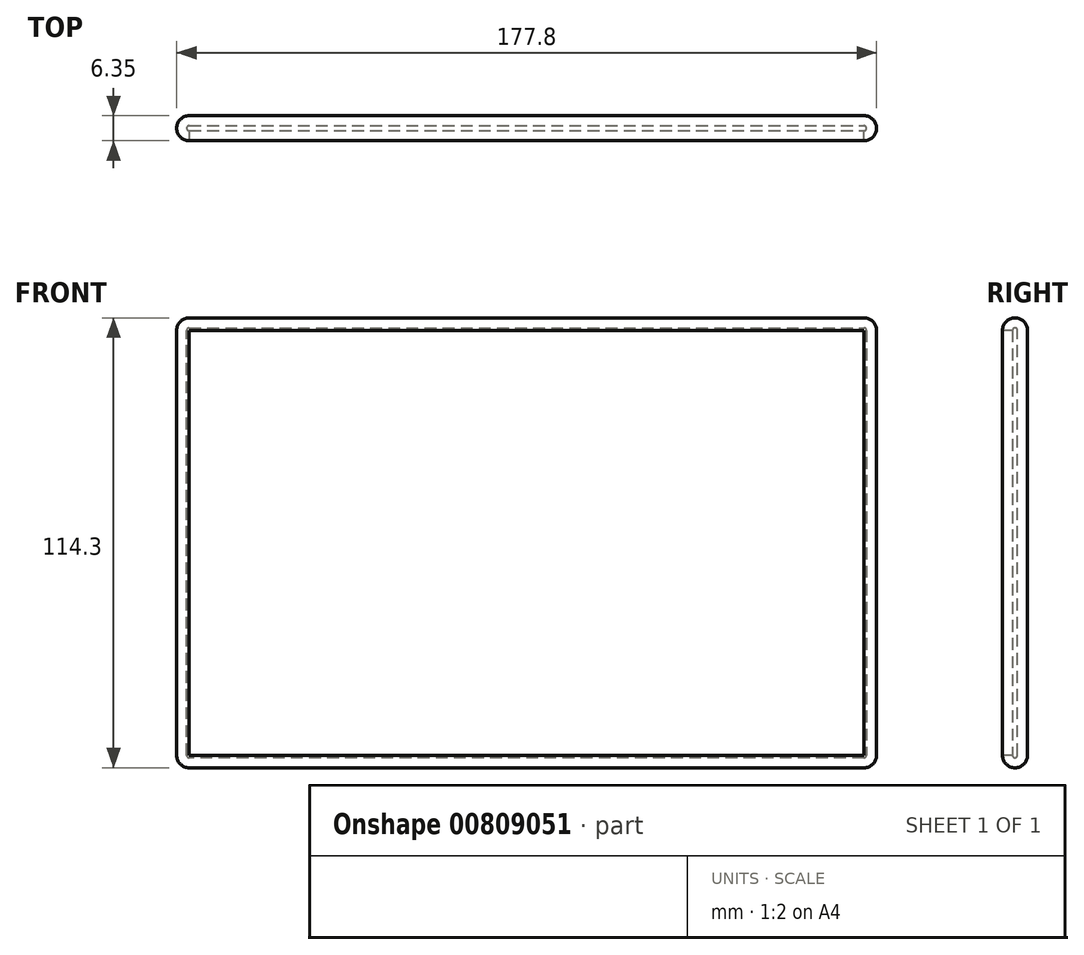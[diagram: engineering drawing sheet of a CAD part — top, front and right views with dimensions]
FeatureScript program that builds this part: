
annotation { "Feature Type Name" : "Feature", "Feature Type Description" : "" }
export const myFeature = defineFeature(function(context is Context, id is Id, definition is map)
    precondition{}
    {
        {
            var Q0;
            Q0=qCreatedBy(makeId("Front.planeOp"),FACE);
            var sketch = newSketch(context, id + "F0", { "sketchPlane" : qUnion([Q0])});
            skLineSegment(sketch, "E0.bottom", {"start": v(-42.92, 86.07) * mm, "end": v(134.88, 86.07) * mm});
            skLineSegment(sketch, "E0.top", {"start": v(-42.92, -28.23) * mm, "end": v(134.88, -28.23) * mm});
            skLineSegment(sketch, "E0.left", {"start": v(-42.92, 86.07) * mm, "end": v(-42.92, -28.23) * mm});
            skLineSegment(sketch, "E0.right", {"start": v(134.88, 86.07) * mm, "end": v(134.88, -28.23) * mm});
            skSolve(sketch);
        }
        {
            var Q0;
            Q0=makeQuery(id+"F0.imprint","IMPRINT",FACE,{"disambiguationData":[TD([[makeQuery(id+"F0.imprint","IMPRINT",EDGE,{"derivedFrom":sQuery(id+"F0.wireOp",EDGE,"E0.bottom")}),-1.0]])]});
            extrude(context, id + "F1", {"entities" : qUnion([Q0]), "depth" : 6.35 * mm, "offsetDistance" : 25.4 * mm});
        }
        {
            var Q0;
            Q0=makeQuery(id+"F1.opExtrude","CAP_EDGE",EDGE,{"disambiguationData":[OSD([sQuery(id+"F0.wireOp",EDGE,"E0.bottom")])],"isStart":true});
            var Q1;
            Q1=makeQuery(id+"F1.opExtrude","SWEPT_EDGE",EDGE,{"disambiguationData":[OSD([sQuery(id+"F0.wireOp",EDGE,"E0.bottom"),sQuery(id+"F0.wireOp",EDGE,"E0.right")])]});
            var Q2;
            Q2=makeQuery(id+"F1.opExtrude","CAP_EDGE",EDGE,{"disambiguationData":[OSD([sQuery(id+"F0.wireOp",EDGE,"E0.bottom")])],"isStart":false});
            var Q3;
            Q3=makeQuery(id+"F1.opExtrude","SWEPT_EDGE",EDGE,{"disambiguationData":[OSD([sQuery(id+"F0.wireOp",EDGE,"E0.bottom"),sQuery(id+"F0.wireOp",EDGE,"E0.left")])]});
            var Q4;
            Q4=makeQuery(id+"F1.opExtrude","CAP_EDGE",EDGE,{"disambiguationData":[OSD([sQuery(id+"F0.wireOp",EDGE,"E0.left")])],"isStart":false});
            var Q5;
            Q5=makeQuery(id+"F1.opExtrude","CAP_EDGE",EDGE,{"disambiguationData":[OSD([sQuery(id+"F0.wireOp",EDGE,"E0.right")])],"isStart":false});
            var Q6;
            Q6=makeQuery(id+"F1.opExtrude","CAP_EDGE",EDGE,{"disambiguationData":[OSD([sQuery(id+"F0.wireOp",EDGE,"E0.right")])],"isStart":true});
            var Q7;
            Q7=makeQuery(id+"F1.opExtrude","CAP_EDGE",EDGE,{"disambiguationData":[OSD([sQuery(id+"F0.wireOp",EDGE,"E0.top")])],"isStart":false});
            var Q8;
            Q8=makeQuery(id+"F1.opExtrude","CAP_EDGE",EDGE,{"disambiguationData":[OSD([sQuery(id+"F0.wireOp",EDGE,"E0.top")])],"isStart":true});
            var Q9;
            Q9=makeQuery(id+"F1.opExtrude","CAP_EDGE",EDGE,{"disambiguationData":[OSD([sQuery(id+"F0.wireOp",EDGE,"E0.left")])],"isStart":true});
            var Q10;
            Q10=makeQuery(id+"F1.opExtrude","SWEPT_EDGE",EDGE,{"disambiguationData":[OSD([sQuery(id+"F0.wireOp",EDGE,"E0.top"),sQuery(id+"F0.wireOp",EDGE,"E0.right")])]});
            var Q11;
            Q11=makeQuery(id+"F1.opExtrude","SWEPT_EDGE",EDGE,{"disambiguationData":[OSD([sQuery(id+"F0.wireOp",EDGE,"E0.top"),sQuery(id+"F0.wireOp",EDGE,"E0.left")])]});
            fillet(context, id + "F2", {"entities" : qUnion([Q0, Q1, Q2, Q3, Q4, Q5, Q6, Q7, Q8, Q9, Q10, Q11]), "radius" : 3.17 * mm, "tangentPropagation" : true, "allowEdgeOverflow" : false});
        }
        {
            var Q0;
            Q0=makeQuery(id+"F1.opExtrude","CAP_FACE",FACE,{"disambiguationData":[OSD([sQuery(id+"F0.wireOp",EDGE,"E0.bottom"),sQuery(id+"F0.wireOp",EDGE,"E0.top"),sQuery(id+"F0.wireOp",EDGE,"E0.left"),sQuery(id+"F0.wireOp",EDGE,"E0.right")])],"isStart":false});
            shell(context, id + "F3", {"entities" : qUnion([Q0]), "thickness" : 2.54 * mm});
        }
    });
